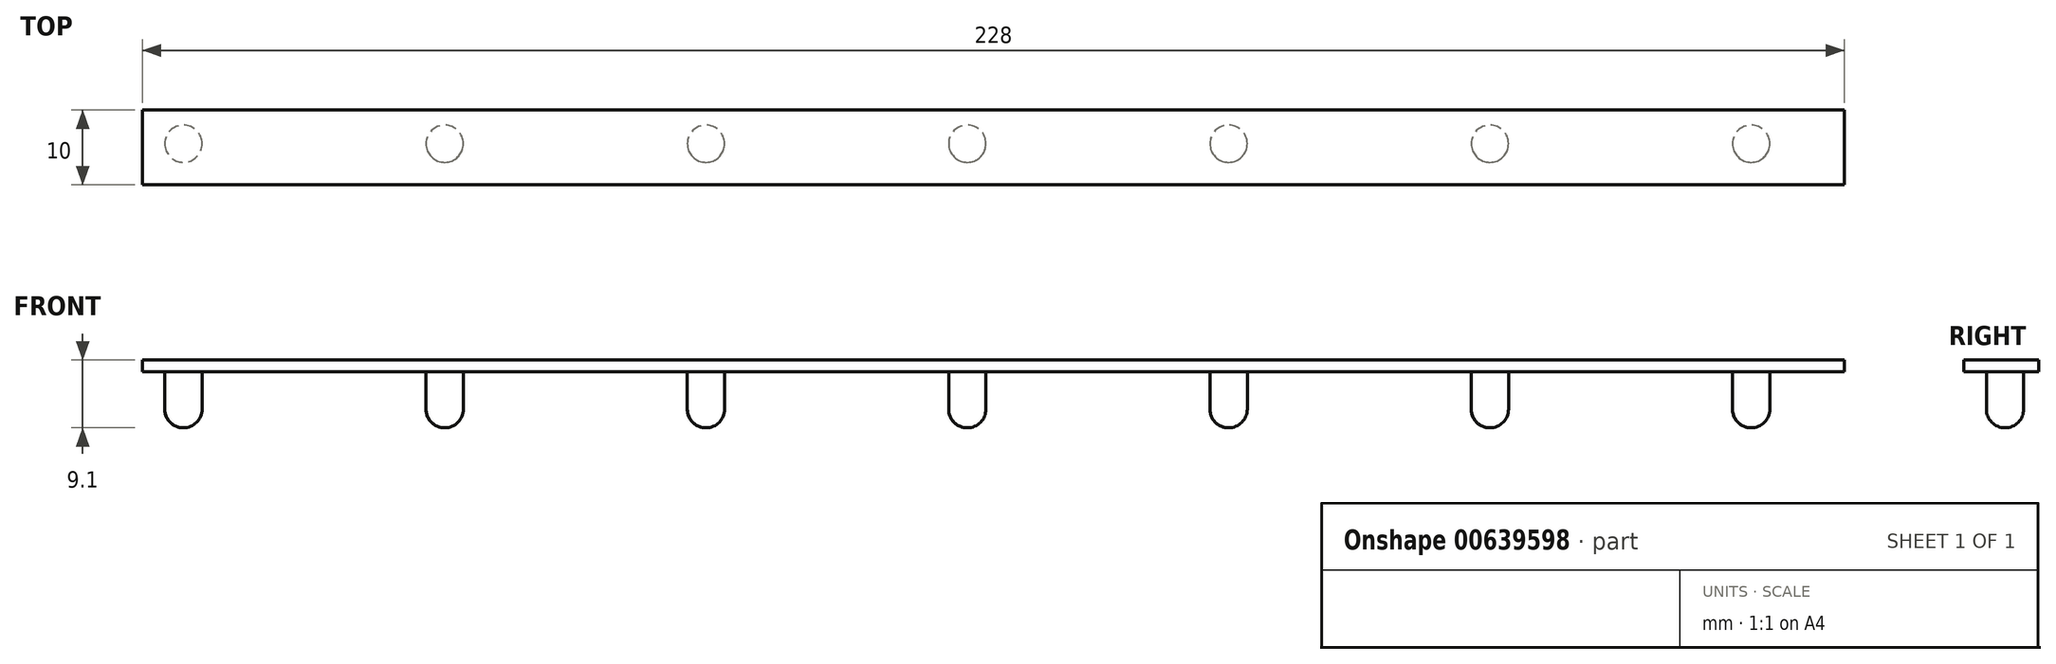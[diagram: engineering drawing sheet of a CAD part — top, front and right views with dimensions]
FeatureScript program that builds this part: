
annotation { "Feature Type Name" : "Feature", "Feature Type Description" : "" }
export const myFeature = defineFeature(function(context is Context, id is Id, definition is map)
    precondition{}
    {
        {
            var Q0;
            Q0=qCreatedBy(makeId("Top.planeOp"),FACE);
            var sketch = newSketch(context, id + "F0", { "sketchPlane" : qUnion([Q0])});
            skLineSegment(sketch, "E0.bottom", {"start": v(-114, 5) * mm, "end": v(114, 5) * mm});
            skLineSegment(sketch, "E0.top", {"start": v(-114, -5) * mm, "end": v(114, -5) * mm});
            skLineSegment(sketch, "E0.left", {"start": v(-114, 5) * mm, "end": v(-114, -5) * mm});
            skLineSegment(sketch, "E0.right", {"start": v(114, 5) * mm, "end": v(114, -5) * mm});
            skPoint(sketch, "E0.middle", {"position": v(0, 0) * mm});
            skSolve(sketch);
        }
        {
            var Q0;
            Q0 = qSketchRegion(id + "F0", true);
            extrude(context, id + "F1", {"entities" : qUnion([Q0]), "depth" : 1.6 * mm, "offsetDistance" : 25 * mm});
        }
        {
            var Q0;
            Q0=makeQuery(id+"F1.opExtrude","CAP_FACE",FACE,{"disambiguationData":[OSD([sQuery(id+"F0.wireOp",EDGE,"E0.bottom"),sQuery(id+"F0.wireOp",EDGE,"E0.top"),sQuery(id+"F0.wireOp",EDGE,"E0.left"),sQuery(id+"F0.wireOp",EDGE,"E0.right")])],"isStart":true});
            var sketch = newSketch(context, id + "F2", { "sketchPlane" : qUnion([Q0])});
            skCircle(sketch, "E1", {"center": v(-108.5, -0.5) * mm, "radius": 2.5 * mm});
            skCircle(sketch, "E2", {"center": v(-73.5, -0.5) * mm, "radius": 2.5 * mm});
            skCircle(sketch, "E3", {"center": v(-38.5, -0.5) * mm, "radius": 2.5 * mm});
            skCircle(sketch, "E4", {"center": v(-3.5, -0.5) * mm, "radius": 2.5 * mm});
            skCircle(sketch, "E5", {"center": v(31.5, -0.5) * mm, "radius": 2.5 * mm});
            skCircle(sketch, "E6", {"center": v(66.5, -0.5) * mm, "radius": 2.5 * mm});
            skCircle(sketch, "E7", {"center": v(101.5, -0.5) * mm, "radius": 2.5 * mm});
            skSolve(sketch);
        }
        {
            var Q0;
            Q0=makeQuery(id+"F2.imprint","IMPRINT",FACE,{"disambiguationData":[TD([[makeQuery(id+"F2.imprint","IMPRINT",EDGE,{"derivedFrom":sQuery(id+"F2.wireOp",EDGE,"E1")}),1.0]])]});
            var Q1;
            Q1=makeQuery(id+"F2.imprint","IMPRINT",FACE,{"disambiguationData":[TD([[makeQuery(id+"F2.imprint","IMPRINT",EDGE,{"derivedFrom":sQuery(id+"F2.wireOp",EDGE,"E2")}),1.0]])]});
            var Q2;
            Q2=makeQuery(id+"F2.imprint","IMPRINT",FACE,{"disambiguationData":[TD([[makeQuery(id+"F2.imprint","IMPRINT",EDGE,{"derivedFrom":sQuery(id+"F2.wireOp",EDGE,"E3")}),1.0]])]});
            var Q3;
            Q3=makeQuery(id+"F2.imprint","IMPRINT",FACE,{"disambiguationData":[TD([[makeQuery(id+"F2.imprint","IMPRINT",EDGE,{"derivedFrom":sQuery(id+"F2.wireOp",EDGE,"E4")}),1.0]])]});
            var Q4;
            Q4=makeQuery(id+"F2.imprint","IMPRINT",FACE,{"disambiguationData":[TD([[makeQuery(id+"F2.imprint","IMPRINT",EDGE,{"derivedFrom":sQuery(id+"F2.wireOp",EDGE,"E5")}),1.0]])]});
            var Q5;
            Q5=makeQuery(id+"F2.imprint","IMPRINT",FACE,{"disambiguationData":[TD([[makeQuery(id+"F2.imprint","IMPRINT",EDGE,{"derivedFrom":sQuery(id+"F2.wireOp",EDGE,"E6")}),1.0]])]});
            var Q6;
            Q6=makeQuery(id+"F2.imprint","IMPRINT",FACE,{"disambiguationData":[TD([[makeQuery(id+"F2.imprint","IMPRINT",EDGE,{"derivedFrom":sQuery(id+"F2.wireOp",EDGE,"E7")}),1.0]])]});
            extrude(context, id + "F3", {"entities" : qUnion([Q0, Q1, Q2, Q3, Q4, Q5, Q6]), "operationType" : NewBodyOperationType.ADD, "depth" : 7.5 * mm, "offsetDistance" : 25 * mm});
        }
        {
            var Q0;
            Q0=makeQuery(id+"F3.opExtrude","CAP_EDGE",EDGE,{"disambiguationData":[OSD([sQuery(id+"F2.wireOp",EDGE,"E1")])],"isStart":false});
            var Q1;
            Q1=makeQuery(id+"F3.opExtrude","CAP_EDGE",EDGE,{"disambiguationData":[OSD([sQuery(id+"F2.wireOp",EDGE,"E2")])],"isStart":false});
            var Q2;
            Q2=makeQuery(id+"F3.opExtrude","CAP_EDGE",EDGE,{"disambiguationData":[OSD([sQuery(id+"F2.wireOp",EDGE,"E3")])],"isStart":false});
            var Q3;
            Q3=makeQuery(id+"F3.opExtrude","CAP_EDGE",EDGE,{"disambiguationData":[OSD([sQuery(id+"F2.wireOp",EDGE,"E4")])],"isStart":false});
            var Q4;
            Q4=makeQuery(id+"F3.opExtrude","CAP_EDGE",EDGE,{"disambiguationData":[OSD([sQuery(id+"F2.wireOp",EDGE,"E5")])],"isStart":false});
            var Q5;
            Q5=makeQuery(id+"F3.opExtrude","CAP_EDGE",EDGE,{"disambiguationData":[OSD([sQuery(id+"F2.wireOp",EDGE,"E6")])],"isStart":false});
            var Q6;
            Q6=makeQuery(id+"F3.opExtrude","CAP_EDGE",EDGE,{"disambiguationData":[OSD([sQuery(id+"F2.wireOp",EDGE,"E7")])],"isStart":false});
            fillet(context, id + "F4", {"entities" : qUnion([Q0, Q1, Q2, Q3, Q4, Q5, Q6]), "radius" : 2.5 * mm, "tangentPropagation" : true, "allowEdgeOverflow" : false});
        }
    });
